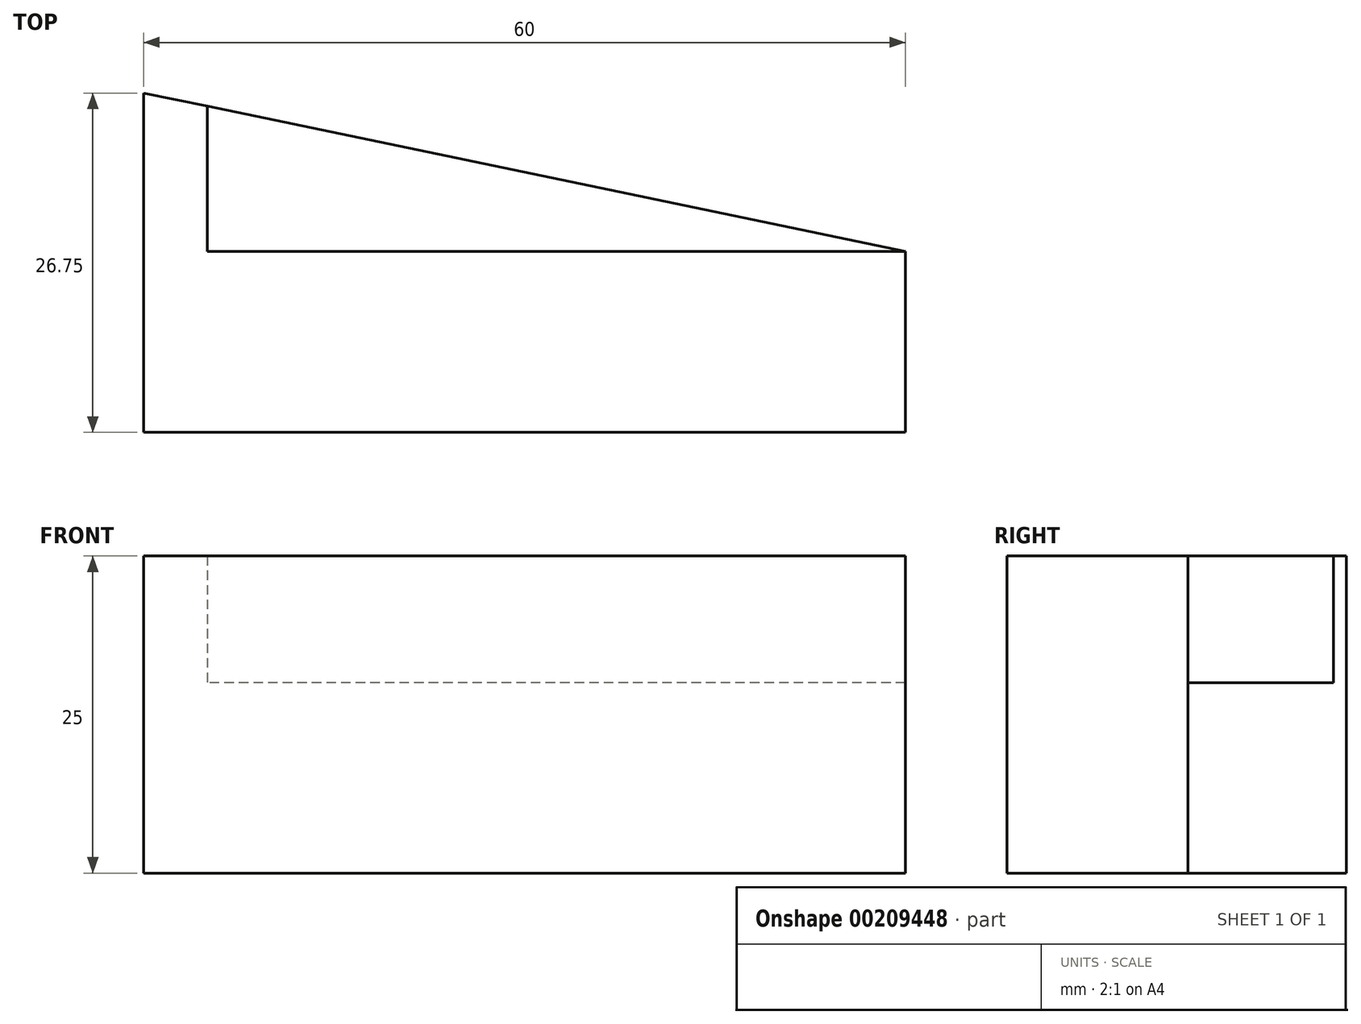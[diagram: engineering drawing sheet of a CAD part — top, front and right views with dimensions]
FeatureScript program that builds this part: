
annotation { "Feature Type Name" : "Feature", "Feature Type Description" : "" }
export const myFeature = defineFeature(function(context is Context, id is Id, definition is map)
    precondition{}
    {
        {
            var Q0;
            Q0=qCreatedBy(makeId("Top.planeOp"),FACE);
            var sketch = newSketch(context, id + "F0", { "sketchPlane" : qUnion([Q0])});
            skLineSegment(sketch, "E0", {"start": v(30, 0) * mm, "end": v(60, 0) * mm});
            skLineSegment(sketch, "E1", {"start": v(60, 0) * mm, "end": v(90, 0) * mm});
            skLineSegment(sketch, "E2", {"start": v(90, 0) * mm, "end": v(90, 18.75) * mm});
            skLineSegment(sketch, "E3", {"start": v(60, 0) * mm, "end": v(60, 12.5) * mm});
            skLineSegment(sketch, "E4", {"start": v(30, 6.25) * mm, "end": v(90, 18.75) * mm});
            skLineSegment(sketch, "E5", {"start": v(30, 0) * mm, "end": v(30, 6.25) * mm});
            skSolve(sketch);
        }
        {
            var Q0;
            Q0=qSketchRegion(id+"F0",true);
            extrude(context, id + "F1", {"entities" : qUnion([Q0]), "depth" : 15 * mm});
        }
        {
            var Q0;
            Q0=makeQuery(id+"F1.opExtrude","CAP_FACE",FACE,{"disambiguationData":[OSD([sQuery(id+"F0.wireOp",EDGE,"E0"),sQuery(id+"F0.wireOp",EDGE,"HZKhCLW9-oDJk-jZ79-Cc5a-FlSk4M4CYGuW"),sQuery(id+"F0.wireOp",EDGE,"E1"),sQuery(id+"F0.wireOp",EDGE,"E2")])],"isStart":false});
            var sketch = newSketch(context, id + "F2", { "sketchPlane" : qUnion([Q0])});
            skLineSegment(sketch, "E6", {"start": v(90, 0) * mm, "end": v(90, 0) * mm});
            skLineSegment(sketch, "E7", {"start": v(90, 0) * mm, "end": v(30, 0) * mm});
            skLineSegment(sketch, "E8", {"start": v(90, 0) * mm, "end": v(90, 18.75) * mm});
            skLineSegment(sketch, "E9.0", {"start": v(85, 6.25) * mm, "end": v(85, 17.7) * mm});
            skLineSegment(sketch, "E10", {"start": v(30, 6.25) * mm, "end": v(85, 6.25) * mm});
            skLineSegment(sketch, "E11", {"start": v(30, 6.25) * mm, "end": v(30, 0) * mm});
            skLineSegment(sketch, "E12", {"start": v(90, 18.75) * mm, "end": v(85, 17.7) * mm});
            skSolve(sketch);
        }
        {
            var Q0;
            Q0=qSketchRegion(id+"F2",true);
            extrude(context, id + "F3", {"entities" : qUnion([Q0]), "operationType" : NewBodyOperationType.ADD, "depth" : 10 * mm});
        }
        {
            var Q0;
            Q0=makeQuery(id+"F3.boolean.opBoolean","MERGE",FACE,{"derivedFrom":[makeQuery(id+"F1.opExtrude","SWEPT_FACE",FACE,{"disambiguationData":[OSD([sQuery(id+"F0.wireOp",EDGE,"E0"),sQuery(id+"F0.wireOp",EDGE,"E1")])]}),makeQuery(id+"F3.opExtrude","SWEPT_FACE",FACE,{"disambiguationData":[OSD([sQuery(id+"F2.wireOp",EDGE,"E7")])]})]});
            extrude(context, id + "F4", {"entities" : qUnion([Q0]), "operationType" : NewBodyOperationType.ADD, "depth" : 3 * mm});
        }
        {
            var Q0;
            Q0=makeQuery(id+"F4.opExtrude","CAP_FACE",FACE,{"disambiguationData":[OSD([sQuery(id+"F0.wireOp",EDGE,"E0"),sQuery(id+"F0.wireOp",EDGE,"E1"),sQuery(id+"F2.wireOp",EDGE,"E7")])],"isStart":false});
            extrude(context, id + "F5", {"entities" : qUnion([Q0]), "operationType" : NewBodyOperationType.ADD, "depth" : 5 * mm});
        }
        {
            var Q0;
            Q0=makeQuery(id+"F1.opExtrude","SWEPT_BODY",BODY,{"disambiguationData":[OSD([sQuery(id+"F0.wireOp",EDGE,"E0"),sQuery(id+"F0.wireOp",EDGE,"E1"),sQuery(id+"F0.wireOp",EDGE,"E2"),sQuery(id+"F0.wireOp",EDGE,"E4"),sQuery(id+"F0.wireOp",EDGE,"E5")])]});
            var Q1;
            Q1=qCreatedBy(makeId("Right.planeOp"),FACE);
            mirror(context, id + "F6", {"entities" : qUnion([Q0]), "mirrorPlane" : qUnion([Q1])});
        }
        {
            var Q0;
            Q0=makeQuery(id+"F1.opExtrude","SWEPT_BODY",BODY,{"disambiguationData":[OSD([sQuery(id+"F0.wireOp",EDGE,"E0"),sQuery(id+"F0.wireOp",EDGE,"E1"),sQuery(id+"F0.wireOp",EDGE,"E2"),sQuery(id+"F0.wireOp",EDGE,"E4"),sQuery(id+"F0.wireOp",EDGE,"E5")])]});
            deleteBodies(context, id + "F7", {"entities" : qUnion([Q0])});
        }
    });
